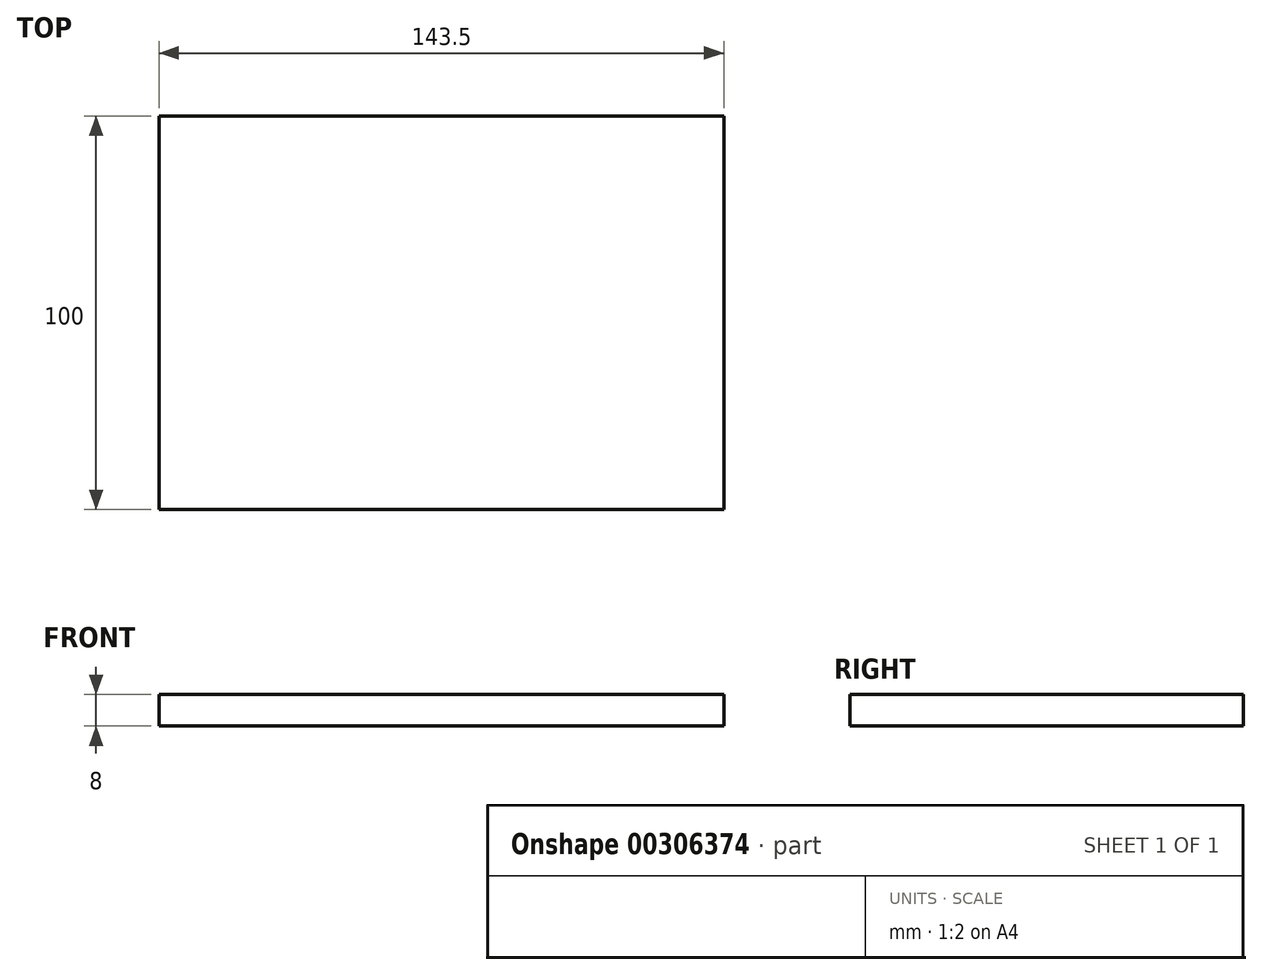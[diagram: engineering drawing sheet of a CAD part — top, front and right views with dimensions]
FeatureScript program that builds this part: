
annotation { "Feature Type Name" : "Feature", "Feature Type Description" : "" }
export const myFeature = defineFeature(function(context is Context, id is Id, definition is map)
    precondition{}
    {
        {
            var Q0;
            Q0=qCreatedBy(makeId("Front.planeOp"),FACE);
            var sketch = newSketch(context, id + "F0", { "sketchPlane" : qUnion([Q0])});
            skLineSegment(sketch, "E0.bottom", {"start": v(-75.16, 8) * mm, "end": v(68.34, 8) * mm});
            skLineSegment(sketch, "E0.top", {"start": v(-75.16, 0) * mm, "end": v(68.34, 0) * mm});
            skLineSegment(sketch, "E0.left", {"start": v(-75.16, 8) * mm, "end": v(-75.16, 0) * mm});
            skLineSegment(sketch, "E0.right", {"start": v(68.34, 8) * mm, "end": v(68.34, 0) * mm});
            skSolve(sketch);
        }
        {
            var Q0;
            Q0=makeQuery(id+"F0.imprint","IMPRINT",FACE,{"disambiguationData":[TD([[makeQuery(id+"F0.imprint","IMPRINT",EDGE,{"derivedFrom":sQuery(id+"F0.wireOp",EDGE,"E0.bottom")}),-1.0]])]});
            extrude(context, id + "F1", {"entities" : qUnion([Q0]), "depth" : 100 * mm});
        }
    });
